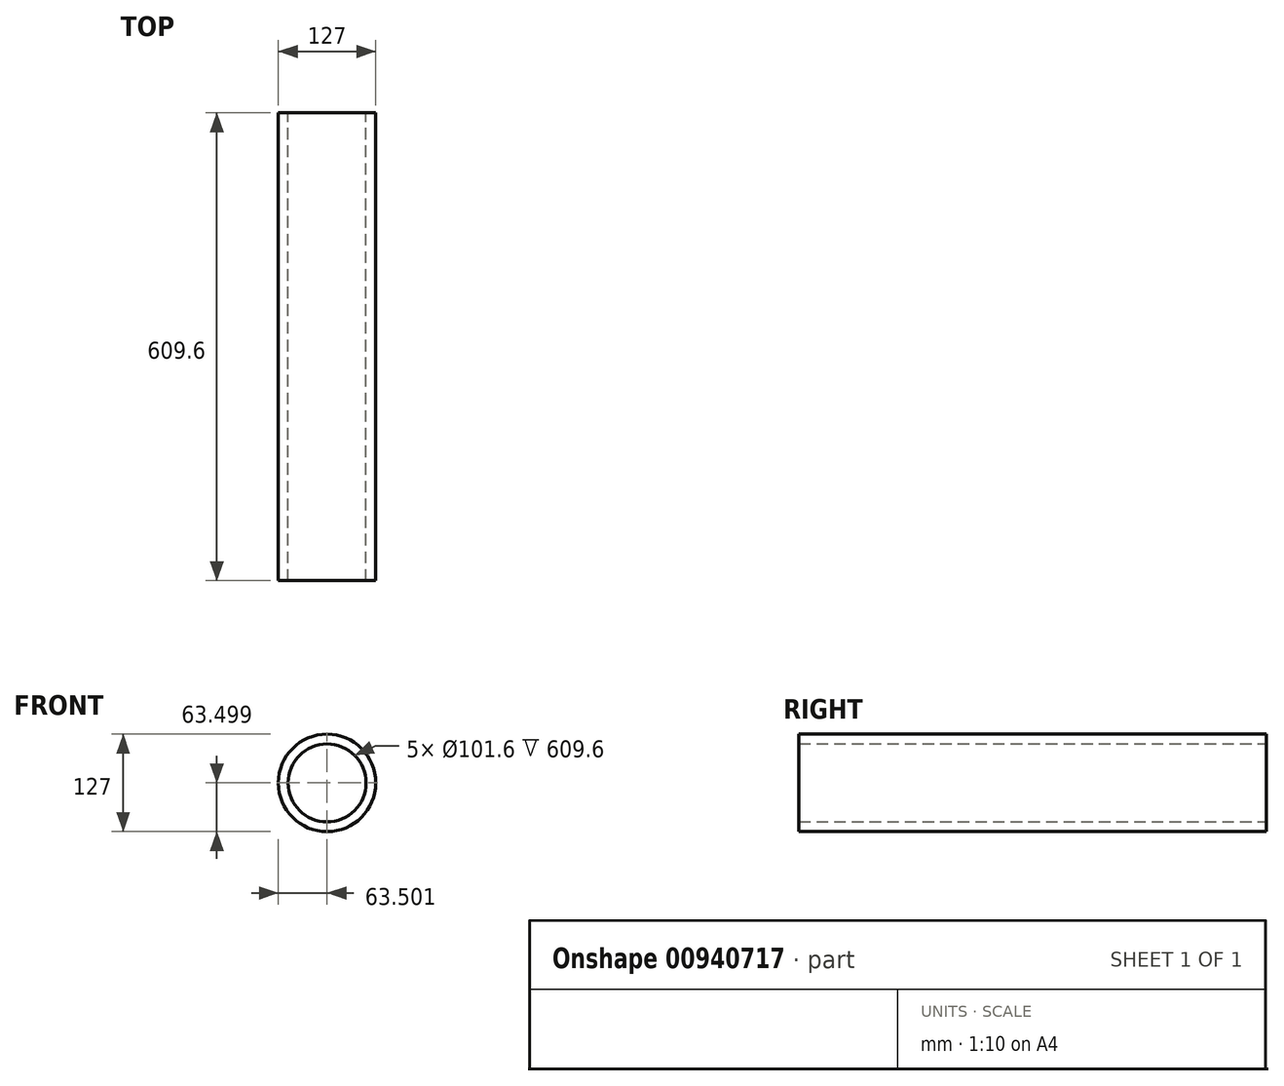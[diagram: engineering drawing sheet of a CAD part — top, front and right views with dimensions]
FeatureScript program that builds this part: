
annotation { "Feature Type Name" : "Feature", "Feature Type Description" : "" }
export const myFeature = defineFeature(function(context is Context, id is Id, definition is map)
    precondition{}
    {
        {
            var Q0;
            Q0=qCreatedBy(makeId("Front.planeOp"),FACE);
            var sketch = newSketch(context, id + "F0", { "sketchPlane" : qUnion([Q0])});
            skCircle(sketch, "E0", {"center": v(-92.15, 45.58) * mm, "radius": 50.8 * mm});
            skCircle(sketch, "E1", {"center": v(-92.15, 45.58) * mm, "radius": 63.5 * mm});
            skSolve(sketch);
        }
        {
            var Q0;
            Q0=makeQuery(id+"F0.imprint","IMPRINT",FACE,{"disambiguationData":[TD([[makeQuery(id+"F0.imprint","IMPRINT",EDGE,{"derivedFrom":sQuery(id+"F0.wireOp",EDGE,"E0")}),-1.0]])]});
            extrude(context, id + "F1", {"entities" : qUnion([Q0]), "depth" : 609.6 * mm, "offsetDistance" : 25.4 * mm});
        }
    });
